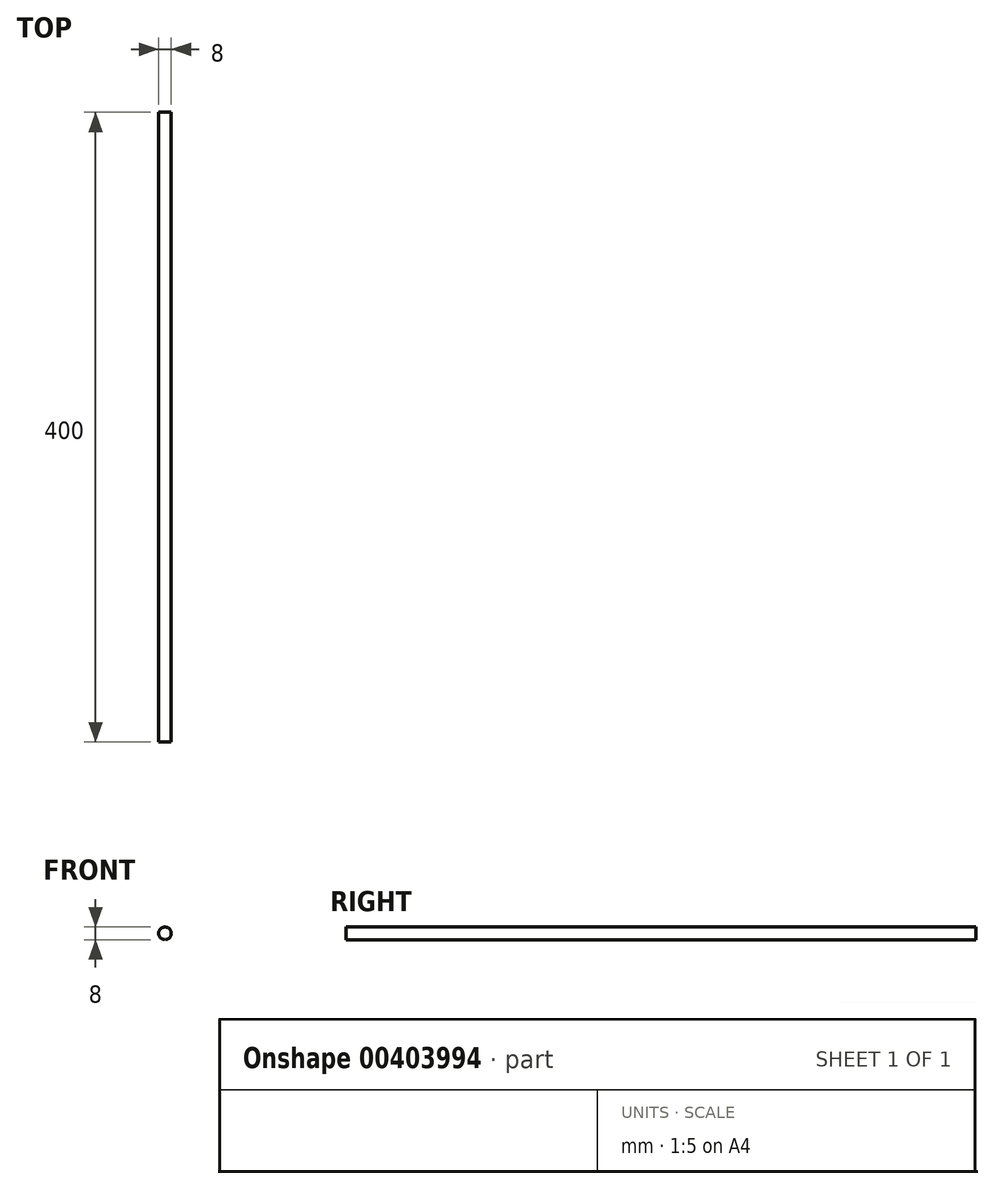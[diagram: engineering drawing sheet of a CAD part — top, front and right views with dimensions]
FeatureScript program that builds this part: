
annotation { "Feature Type Name" : "Feature", "Feature Type Description" : "" }
export const myFeature = defineFeature(function(context is Context, id is Id, definition is map)
    precondition{}
    {
        {
            var Q0;
            Q0=qCreatedBy(makeId("Front.planeOp"),FACE);
            var sketch = newSketch(context, id + "F0", { "sketchPlane" : qUnion([Q0])});
            skCircle(sketch, "E0", {"center": v(0, 0) * mm, "radius": 4 * mm});
            skSolve(sketch);
        }
        {
            var Q0;
            Q0=makeQuery(id+"F0.imprint","IMPRINT",FACE,{"disambiguationData":[TD([[makeQuery(id+"F0.imprint","IMPRINT",EDGE,{"derivedFrom":sQuery(id+"F0.wireOp",EDGE,"E0")}),1.0]])]});
            extrude(context, id + "F1", {"entities" : qUnion([Q0]), "depth" : 400 * mm});
        }
    });
